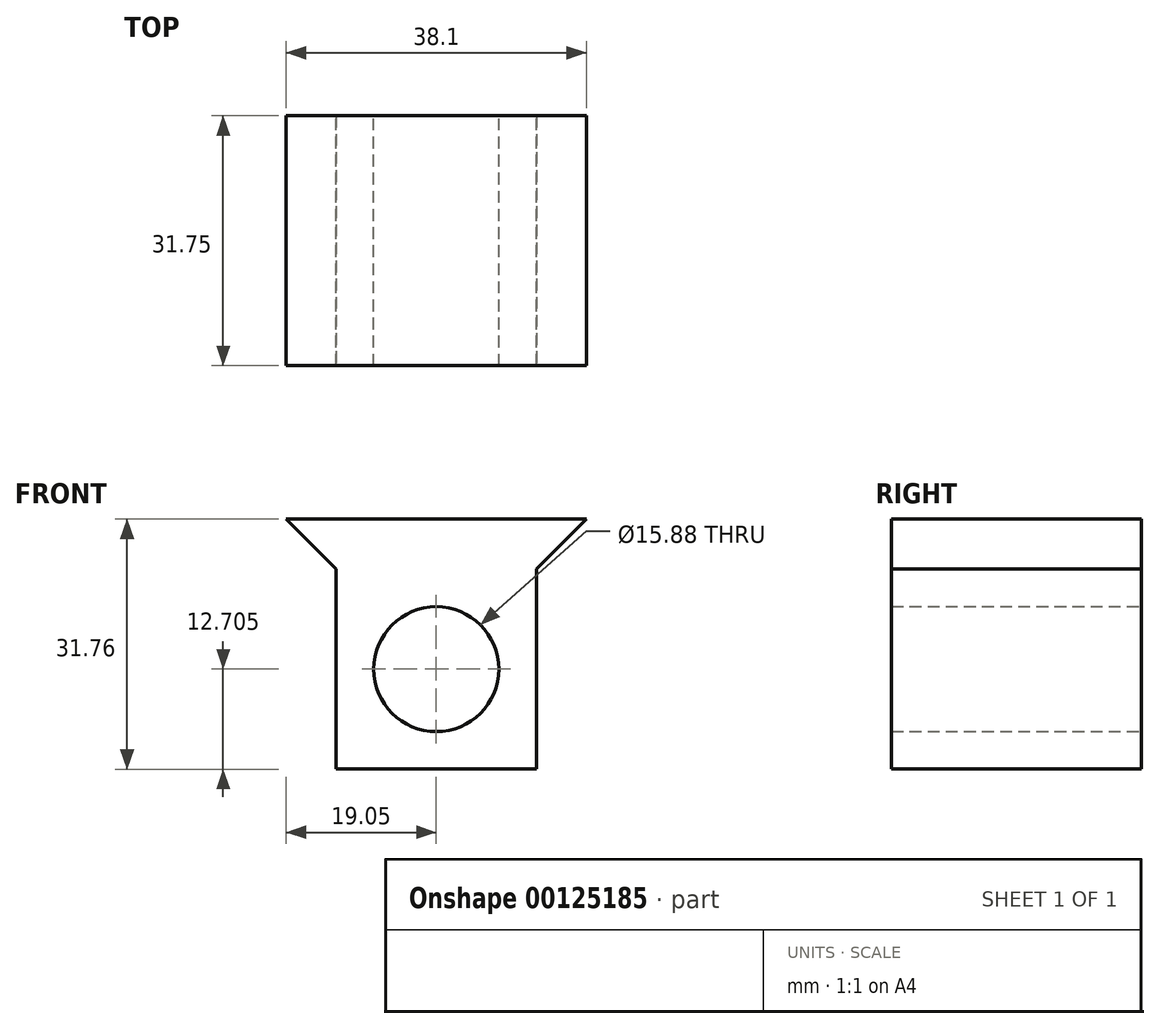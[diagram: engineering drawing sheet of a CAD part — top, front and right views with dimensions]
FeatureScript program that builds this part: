
annotation { "Feature Type Name" : "Feature", "Feature Type Description" : "" }
export const myFeature = defineFeature(function(context is Context, id is Id, definition is map)
    precondition{}
    {
        {
            var Q0;
            Q0=qCreatedBy(makeId("Front.planeOp"),FACE);
            var sketch = newSketch(context, id + "F0", { "sketchPlane" : qUnion([Q0])});
            skLineSegment(sketch, "E0.bottom", {"start": v(12.7, 15.88) * mm, "end": v(-12.7, 15.88) * mm});
            skLineSegment(sketch, "E0.top", {"start": v(12.7, -15.88) * mm, "end": v(-12.7, -15.88) * mm});
            skLineSegment(sketch, "E0.left", {"start": v(12.7, 15.88) * mm, "end": v(12.7, -15.88) * mm});
            skLineSegment(sketch, "E0.right", {"start": v(-12.7, 15.88) * mm, "end": v(-12.7, -15.88) * mm});
            skPoint(sketch, "E0.middle", {"position": v(0, 0) * mm});
            skSolve(sketch);
        }
        {
            var Q0;
            Q0=makeQuery(id+"F0.imprint","IMPRINT",FACE,{"disambiguationData":[TD([[makeQuery(id+"F0.imprint","IMPRINT",EDGE,{"derivedFrom":sQuery(id+"F0.wireOp",EDGE,"E0.bottom")}),1.0]])]});
            extrude(context, id + "F1", {"entities" : qUnion([Q0]), "depth" : 31.75 * mm});
        }
        {
            var Q0;
            Q0=makeQuery(id+"F1.opExtrude","CAP_FACE",FACE,{"disambiguationData":[OSD([sQuery(id+"F0.wireOp",EDGE,"E0.bottom"),sQuery(id+"F0.wireOp",EDGE,"E0.top"),sQuery(id+"F0.wireOp",EDGE,"E0.left"),sQuery(id+"F0.wireOp",EDGE,"E0.right")])],"isStart":true});
            var sketch = newSketch(context, id + "F2", { "sketchPlane" : qUnion([Q0])});
            skCircle(sketch, "E1", {"center": v(0, -3.18) * mm, "radius": 7.94 * mm});
            skLineSegment(sketch, "E2", {"start": v(0, 20.62) * mm, "end": v(0, -25.94) * mm, "construction": true});
            skSolve(sketch);
        }
        {
            var Q0;
            Q0=makeQuery(id+"F2.imprint","IMPRINT",FACE,{"disambiguationData":[TD([[makeQuery(id+"F2.imprint","IMPRINT",EDGE,{"derivedFrom":sQuery(id+"F2.wireOp",EDGE,"E1")}),1.0]])]});
            var Q1;
            Q1=makeQuery(id+"F1.opExtrude","CAP_FACE",FACE,{"disambiguationData":[OSD([sQuery(id+"F0.wireOp",EDGE,"E0.bottom"),sQuery(id+"F0.wireOp",EDGE,"E0.top"),sQuery(id+"F0.wireOp",EDGE,"E0.left"),sQuery(id+"F0.wireOp",EDGE,"E0.right")])],"isStart":false});
            extrude(context, id + "F3", {"entities" : qUnion([Q0]), "operationType" : NewBodyOperationType.REMOVE, "endBound" : BoundingType.UP_TO_SURFACE, "oppositeDirection" : true, "endBoundEntityFace" : qUnion([Q1]), "depth" : 25.4 * mm});
        }
        {
            var Q0;
            Q0=makeQuery(id+"F1.opExtrude","CAP_FACE",FACE,{"disambiguationData":[OSD([sQuery(id+"F0.wireOp",EDGE,"E0.bottom"),sQuery(id+"F0.wireOp",EDGE,"E0.top"),sQuery(id+"F0.wireOp",EDGE,"E0.left"),sQuery(id+"F0.wireOp",EDGE,"E0.right")])],"isStart":true});
            var sketch = newSketch(context, id + "F4", { "sketchPlane" : qUnion([Q0])});
            skLineSegment(sketch, "E3", {"start": v(-19.05, 15.88) * mm, "end": v(19.05, 15.88) * mm});
            skLineSegment(sketch, "E4", {"start": v(19.05, 15.88) * mm, "end": v(12.7, 9.53) * mm});
            skLineSegment(sketch, "E5", {"start": v(12.7, 9.53) * mm, "end": v(-12.7, 9.53) * mm});
            skLineSegment(sketch, "E6", {"start": v(-12.7, 9.53) * mm, "end": v(-19.05, 15.88) * mm});
            skSolve(sketch);
        }
        {
            var Q0;
            Q0 = qSketchRegion(id + "F4", true);
            var Q1;
            Q1=makeQuery(id+"F1.opExtrude","CAP_FACE",FACE,{"disambiguationData":[OSD([sQuery(id+"F0.wireOp",EDGE,"E0.bottom"),sQuery(id+"F0.wireOp",EDGE,"E0.top"),sQuery(id+"F0.wireOp",EDGE,"E0.left"),sQuery(id+"F0.wireOp",EDGE,"E0.right")])],"isStart":false});
            extrude(context, id + "F5", {"entities" : qUnion([Q0]), "operationType" : NewBodyOperationType.ADD, "endBound" : BoundingType.UP_TO_SURFACE, "oppositeDirection" : true, "endBoundEntityFace" : qUnion([Q1]), "depth" : 25.4 * mm});
        }
    });
